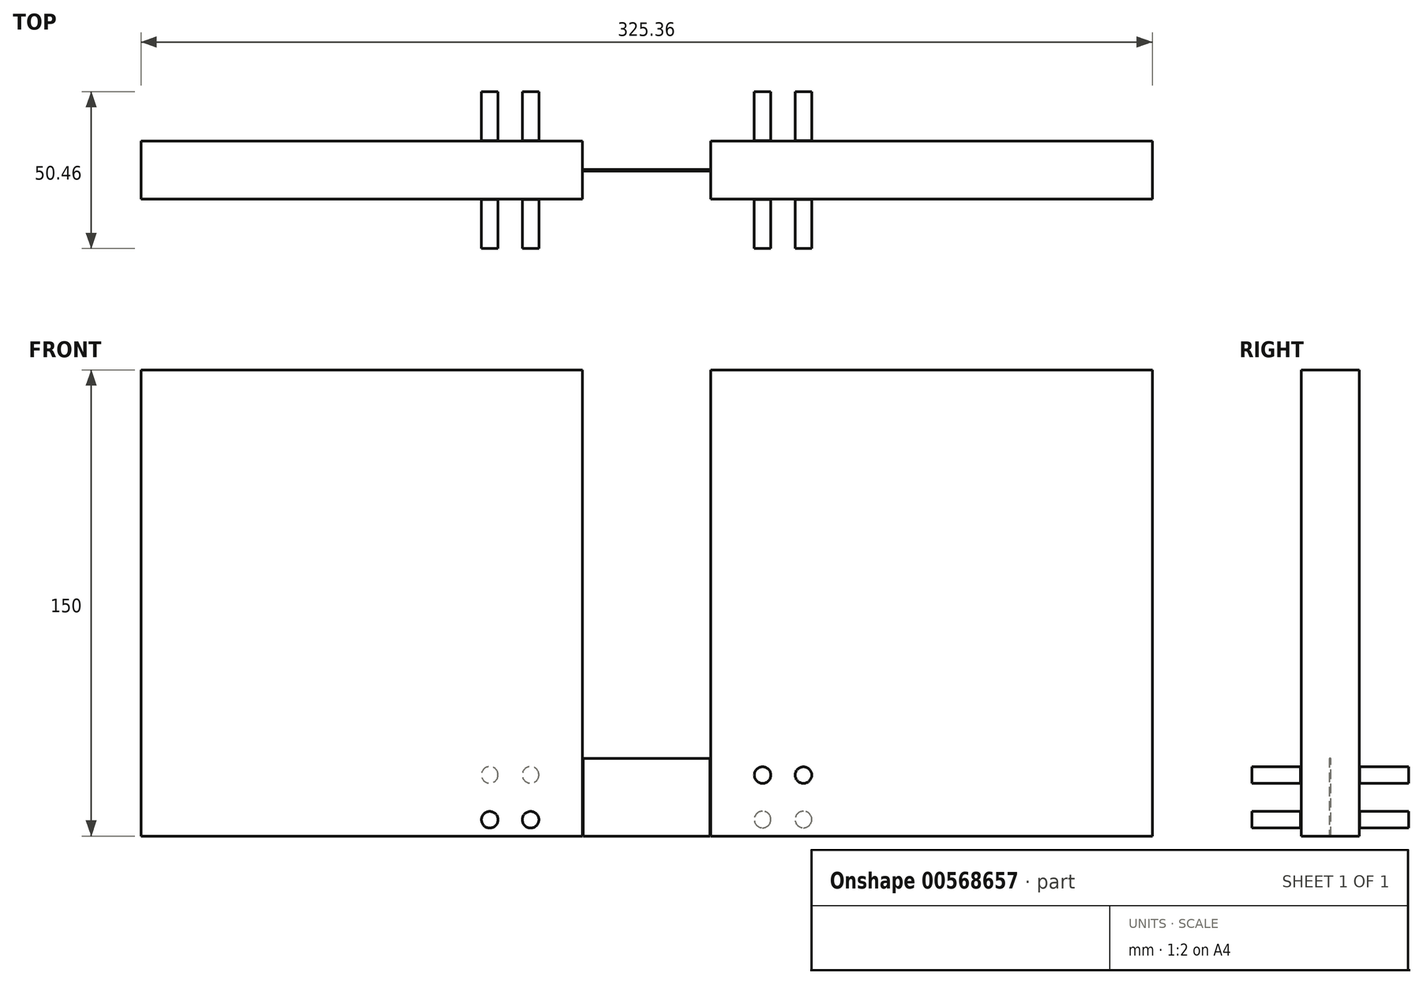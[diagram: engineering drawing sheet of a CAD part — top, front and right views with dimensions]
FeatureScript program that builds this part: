
annotation { "Feature Type Name" : "Feature", "Feature Type Description" : "" }
export const myFeature = defineFeature(function(context is Context, id is Id, definition is map)
    precondition{}
    {
        {
            var Q0;
            Q0=qCreatedBy(makeId("Top.planeOp"),FACE);
            var sketch = newSketch(context, id + "F0", { "sketchPlane" : qUnion([Q0])});
            skLineSegment(sketch, "E0.left", {"start": v(-20.37, 9.5) * mm, "end": v(-20.37, -9.5) * mm});
            skLineSegment(sketch, "E0.right", {"start": v(20.37, 9.5) * mm, "end": v(20.37, -9.5) * mm});
            skPoint(sketch, "E0.middle", {"position": v(0, 0) * mm});
            skLineSegment(sketch, "E1.bottom", {"start": v(-60.65, 25.23) * mm, "end": v(0, 25.23) * mm});
            skLineSegment(sketch, "E1.top", {"start": v(-60.65, 9.5) * mm, "end": v(-20.37, 9.5) * mm});
            skLineSegment(sketch, "E1.left", {"start": v(-60.65, 25.23) * mm, "end": v(-60.65, 9.5) * mm});
            skLineSegment(sketch, "E2.MirrorCS", {"start": v(60.65, 25.23) * mm, "end": v(0, 25.23) * mm});
            skLineSegment(sketch, "E3.MirrorCS", {"start": v(60.65, 9.5) * mm, "end": v(20.37, 9.5) * mm});
            skLineSegment(sketch, "E4.MirrorCS", {"start": v(60.65, 25.23) * mm, "end": v(60.65, 9.5) * mm});
            skLineSegment(sketch, "E5.MirrorCS", {"start": v(-60.65, -9.5) * mm, "end": v(-20.37, -9.5) * mm});
            skLineSegment(sketch, "E6.MirrorCS", {"start": v(60.65, -9.5) * mm, "end": v(20.37, -9.5) * mm});
            skLineSegment(sketch, "E7.MirrorCS", {"start": v(60.65, -25.23) * mm, "end": v(60.65, -9.5) * mm});
            skLineSegment(sketch, "E8.MirrorCS", {"start": v(60.65, -25.23) * mm, "end": v(0, -25.23) * mm});
            skLineSegment(sketch, "E9.MirrorCS", {"start": v(-60.65, -25.23) * mm, "end": v(0, -25.23) * mm});
            skLineSegment(sketch, "E10.MirrorCS", {"start": v(-60.65, -25.23) * mm, "end": v(-60.65, -9.5) * mm});
            skPoint(sketch, "E11.orphan", {"position": v(0, -9.5) * mm});
            skPoint(sketch, "E1.right.end.orphan", {"position": v(0, 9.5) * mm});
            skSolve(sketch);
        }
        {
            var Q0;
            Q0=makeQuery(id+"F0.imprint","IMPRINT",FACE,{"disambiguationData":[TD([[makeQuery(id+"F0.imprint","IMPRINT",EDGE,{"derivedFrom":sQuery(id+"F0.wireOp",EDGE,"E0.left")}),1.0]])]});
            extrude(context, id + "F1", {"entities" : qUnion([Q0]), "depth" : 25 * mm, "offsetDistance" : 25 * mm});
        }
        {
            var Q0;
            Q0=makeQuery(id+"F1.opExtrude","SWEPT_FACE",FACE,{"disambiguationData":[OSD([sQuery(id+"F0.wireOp",EDGE,"E1.bottom"),sQuery(id+"F0.wireOp",EDGE,"E2.MirrorCS")])]});
            var sketch = newSketch(context, id + "F2", { "sketchPlane" : qUnion([Q0])});
            skCircle(sketch, "E12", {"center": v(50.46, 5.32) * mm, "radius": 2.67 * mm});
            skCircle(sketch, "E13", {"center": v(37.32, 5.32) * mm, "radius": 2.67 * mm});
            skCircle(sketch, "E14.MirrorC", {"center": v(50.46, 19.68) * mm, "radius": 2.67 * mm});
            skCircle(sketch, "E15.MirrorC", {"center": v(37.32, 19.68) * mm, "radius": 2.67 * mm});
            skCircle(sketch, "E16.MirrorC", {"center": v(-50.46, 5.32) * mm, "radius": 2.67 * mm});
            skCircle(sketch, "E17.MirrorC", {"center": v(-37.32, 19.68) * mm, "radius": 2.67 * mm});
            skCircle(sketch, "E18.MirrorC", {"center": v(-37.32, 5.32) * mm, "radius": 2.67 * mm});
            skCircle(sketch, "E19.MirrorC", {"center": v(-50.46, 19.68) * mm, "radius": 2.67 * mm});
            skSolve(sketch);
        }
        {
            var Q0;
            Q0=makeQuery(id+"F2.imprint","IMPRINT",FACE,{"disambiguationData":[TD([[makeQuery(id+"F2.imprint","IMPRINT",EDGE,{"derivedFrom":sQuery(id+"F2.wireOp",EDGE,"E12")}),1.0]])]});
            var Q1;
            Q1=makeQuery(id+"F2.imprint","IMPRINT",FACE,{"disambiguationData":[TD([[makeQuery(id+"F2.imprint","IMPRINT",EDGE,{"derivedFrom":sQuery(id+"F2.wireOp",EDGE,"E13")}),1.0]])]});
            var Q2;
            Q2=makeQuery(id+"F2.imprint","IMPRINT",FACE,{"disambiguationData":[TD([[makeQuery(id+"F2.imprint","IMPRINT",EDGE,{"derivedFrom":sQuery(id+"F2.wireOp",EDGE,"E14.MirrorC")}),-1.0]])]});
            var Q3;
            Q3=makeQuery(id+"F2.imprint","IMPRINT",FACE,{"disambiguationData":[TD([[makeQuery(id+"F2.imprint","IMPRINT",EDGE,{"derivedFrom":sQuery(id+"F2.wireOp",EDGE,"E15.MirrorC")}),-1.0]])]});
            var Q4;
            Q4=makeQuery(id+"F2.imprint","IMPRINT",FACE,{"disambiguationData":[TD([[makeQuery(id+"F2.imprint","IMPRINT",EDGE,{"derivedFrom":sQuery(id+"F2.wireOp",EDGE,"E18.MirrorC")}),-1.0]])]});
            var Q5;
            Q5=makeQuery(id+"F2.imprint","IMPRINT",FACE,{"disambiguationData":[TD([[makeQuery(id+"F2.imprint","IMPRINT",EDGE,{"derivedFrom":sQuery(id+"F2.wireOp",EDGE,"E16.MirrorC")}),-1.0]])]});
            var Q6;
            Q6=makeQuery(id+"F2.imprint","IMPRINT",FACE,{"disambiguationData":[TD([[makeQuery(id+"F2.imprint","IMPRINT",EDGE,{"derivedFrom":sQuery(id+"F2.wireOp",EDGE,"E19.MirrorC")}),1.0]])]});
            var Q7;
            Q7=makeQuery(id+"F2.imprint","IMPRINT",FACE,{"disambiguationData":[TD([[makeQuery(id+"F2.imprint","IMPRINT",EDGE,{"derivedFrom":sQuery(id+"F2.wireOp",EDGE,"E17.MirrorC")}),1.0]])]});
            extrude(context, id + "F3", {"entities" : qUnion([Q0, Q1, Q2, Q3, Q4, Q5, Q6, Q7]), "operationType" : NewBodyOperationType.REMOVE, "oppositeDirection" : true, "depth" : 25 * mm, "offsetDistance" : 25 * mm});
        }
        {
            var Q0;
            Q0=makeQuery(id+"F1.opExtrude","SWEPT_FACE",FACE,{"disambiguationData":[OSD([sQuery(id+"F0.wireOp",EDGE,"E8.MirrorCS"),sQuery(id+"F0.wireOp",EDGE,"E9.MirrorCS")])]});
            var sketch = newSketch(context, id + "F4", { "sketchPlane" : qUnion([Q0])});
            skCircle(sketch, "E20", {"center": v(50.46, 5.26) * mm, "radius": 2.67 * mm});
            skCircle(sketch, "E21", {"center": v(37.32, 5.26) * mm, "radius": 2.67 * mm});
            skCircle(sketch, "E22.MirrorC", {"center": v(50.46, 19.62) * mm, "radius": 2.67 * mm});
            skCircle(sketch, "E23.MirrorC", {"center": v(37.32, 19.62) * mm, "radius": 2.67 * mm});
            skCircle(sketch, "E24.MirrorC", {"center": v(-50.46, 5.26) * mm, "radius": 2.67 * mm});
            skCircle(sketch, "E25.MirrorC", {"center": v(-37.32, 19.62) * mm, "radius": 2.67 * mm});
            skCircle(sketch, "E26.MirrorC", {"center": v(-37.32, 5.26) * mm, "radius": 2.67 * mm});
            skCircle(sketch, "E27.MirrorC", {"center": v(-50.46, 19.62) * mm, "radius": 2.67 * mm});
            skSolve(sketch);
        }
        {
            var Q0;
            Q0=makeQuery(id+"F4.imprint","IMPRINT",FACE,{"disambiguationData":[TD([[makeQuery(id+"F4.imprint","IMPRINT",EDGE,{"derivedFrom":sQuery(id+"F4.wireOp",EDGE,"E20")}),1.0]])]});
            var Q1;
            Q1=makeQuery(id+"F4.imprint","IMPRINT",FACE,{"disambiguationData":[TD([[makeQuery(id+"F4.imprint","IMPRINT",EDGE,{"derivedFrom":sQuery(id+"F4.wireOp",EDGE,"E22.MirrorC")}),-1.0]])]});
            var Q2;
            Q2=makeQuery(id+"F4.imprint","IMPRINT",FACE,{"disambiguationData":[TD([[makeQuery(id+"F4.imprint","IMPRINT",EDGE,{"derivedFrom":sQuery(id+"F4.wireOp",EDGE,"E21")}),1.0]])]});
            var Q3;
            Q3=makeQuery(id+"F4.imprint","IMPRINT",FACE,{"disambiguationData":[TD([[makeQuery(id+"F4.imprint","IMPRINT",EDGE,{"derivedFrom":sQuery(id+"F4.wireOp",EDGE,"E23.MirrorC")}),-1.0]])]});
            var Q4;
            Q4=makeQuery(id+"F4.imprint","IMPRINT",FACE,{"disambiguationData":[TD([[makeQuery(id+"F4.imprint","IMPRINT",EDGE,{"derivedFrom":sQuery(id+"F4.wireOp",EDGE,"E26.MirrorC")}),-1.0]])]});
            var Q5;
            Q5=makeQuery(id+"F4.imprint","IMPRINT",FACE,{"disambiguationData":[TD([[makeQuery(id+"F4.imprint","IMPRINT",EDGE,{"derivedFrom":sQuery(id+"F4.wireOp",EDGE,"E25.MirrorC")}),1.0]])]});
            var Q6;
            Q6=makeQuery(id+"F4.imprint","IMPRINT",FACE,{"disambiguationData":[TD([[makeQuery(id+"F4.imprint","IMPRINT",EDGE,{"derivedFrom":sQuery(id+"F4.wireOp",EDGE,"E24.MirrorC")}),-1.0]])]});
            var Q7;
            Q7=makeQuery(id+"F4.imprint","IMPRINT",FACE,{"disambiguationData":[TD([[makeQuery(id+"F4.imprint","IMPRINT",EDGE,{"derivedFrom":sQuery(id+"F4.wireOp",EDGE,"E27.MirrorC")}),1.0]])]});
            extrude(context, id + "F5", {"entities" : qUnion([Q0, Q1, Q2, Q3, Q4, Q5, Q6, Q7]), "operationType" : NewBodyOperationType.REMOVE, "oppositeDirection" : true, "depth" : 25 * mm, "offsetDistance" : 25 * mm});
        }
        {
            var Q0;
            Q0=qCreatedBy(makeId("Top.planeOp"),FACE);
            var sketch = newSketch(context, id + "F6", { "sketchPlane" : qUnion([Q0])});
            skLineSegment(sketch, "E28.bottom", {"start": v(-20.6, 9.42) * mm, "end": v(-162.68, 9.42) * mm});
            skLineSegment(sketch, "E28.top", {"start": v(-20.6, -9.24) * mm, "end": v(-162.68, -9.24) * mm});
            skLineSegment(sketch, "E28.left", {"start": v(-20.6, 9.42) * mm, "end": v(-20.6, -9.24) * mm});
            skLineSegment(sketch, "E28.right", {"start": v(-162.68, 9.42) * mm, "end": v(-162.68, -9.24) * mm});
            skLineSegment(sketch, "E29.MirrorCS", {"start": v(20.6, 9.42) * mm, "end": v(20.6, -9.24) * mm});
            skLineSegment(sketch, "E30.MirrorCS", {"start": v(20.6, 9.42) * mm, "end": v(162.68, 9.42) * mm});
            skLineSegment(sketch, "E31.MirrorCS", {"start": v(20.6, -9.24) * mm, "end": v(162.68, -9.24) * mm});
            skLineSegment(sketch, "E32.MirrorCS", {"start": v(162.68, 9.42) * mm, "end": v(162.68, -9.24) * mm});
            skSolve(sketch);
        }
        {
            var Q0;
            Q0=makeQuery(id+"F6.imprint","IMPRINT",FACE,{"disambiguationData":[TD([[makeQuery(id+"F6.imprint","IMPRINT",EDGE,{"derivedFrom":sQuery(id+"F6.wireOp",EDGE,"E28.bottom")}),1.0]])]});
            extrude(context, id + "F7", {"entities" : qUnion([Q0]), "depth" : 150 * mm, "offsetDistance" : 25 * mm});
        }
        {
            var Q0;
            Q0=makeQuery(id+"F6.imprint","IMPRINT",FACE,{"disambiguationData":[TD([[makeQuery(id+"F6.imprint","IMPRINT",EDGE,{"derivedFrom":sQuery(id+"F6.wireOp",EDGE,"E29.MirrorCS")}),1.0]])]});
            extrude(context, id + "F8", {"entities" : qUnion([Q0]), "depth" : 150 * mm, "offsetDistance" : 25 * mm});
        }
    });
